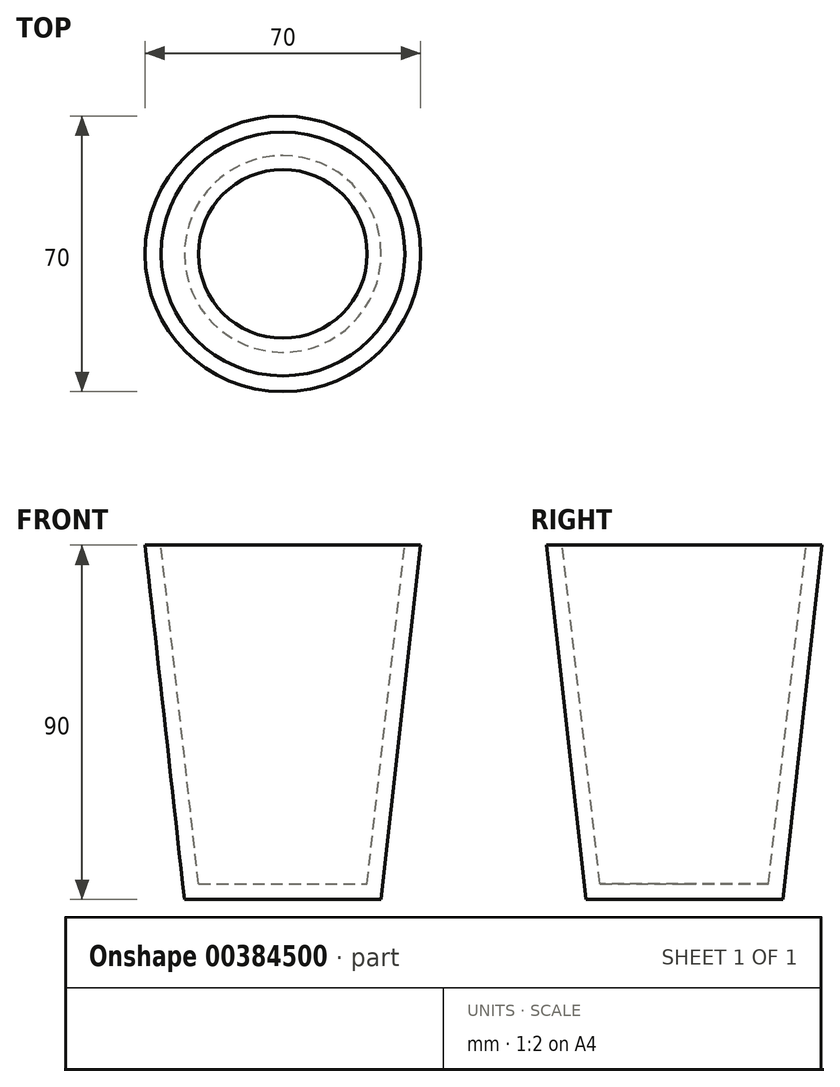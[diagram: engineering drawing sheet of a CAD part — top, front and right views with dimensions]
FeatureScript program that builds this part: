
annotation { "Feature Type Name" : "Feature", "Feature Type Description" : "" }
export const myFeature = defineFeature(function(context is Context, id is Id, definition is map)
    precondition{}
    {
        {
            var Q0;
            Q0=qCreatedBy(makeId("Front.planeOp"),FACE);
            var sketch = newSketch(context, id + "F0", { "sketchPlane" : qUnion([Q0])});
            skLineSegment(sketch, "E0", {"start": v(0, 0) * mm, "end": v(25, 0) * mm});
            skLineSegment(sketch, "E1", {"start": v(25, 0) * mm, "end": v(35, 90) * mm});
            skLineSegment(sketch, "E2", {"start": v(0, 4) * mm, "end": v(21.42, 4) * mm});
            skLineSegment(sketch, "E3", {"start": v(0, 4) * mm, "end": v(0, 0) * mm});
            skLineSegment(sketch, "E4", {"start": v(21.42, 4) * mm, "end": v(30.98, 90) * mm});
            skLineSegment(sketch, "E5", {"start": v(30.98, 90) * mm, "end": v(35, 90) * mm});
            skLineSegment(sketch, "E6", {"start": v(0, -8.74) * mm, "end": v(0, 98.7) * mm, "construction": true});
            skSolve(sketch);
        }
        {
            var Q0;
            Q0 = qSketchRegion(id + "F0", true);
            var Q1;
            Q1=sQuery(id+"F0.wireOp",EDGE,"E6");
            revolve(context, id + "F1", {"entities" : qUnion([Q0]), "axis" : qUnion([Q1]), "revolveType" : RevolveType.FULL});
        }
    });
